# Revit family: HPL-BA-300-xxxx-xxx-PC
name_source: partatom
category: Oprawy oświetleniowe
revit_build: Autodesk Revit 2017 (Build: 20190507_1515(x64)
units: mm (PartAtom-declared; Revit-internal decimal feet)

## family parameters
Numer OmniClass = 23.80.70.11
Obiekt nadrzędny = Powierzchnia
Punkt obliczania pomieszczeń = Nie
Tnij formami wycięć po wczytaniu = Nie
Typ części = Normalny
Tytuł OmniClass = Luminaries for Internal Lighting
Współdzielony = Nie
Wymiar okrągłego złącza = Użyj średnicy
Źródło światła = Tak

## types (12) — shared parameters
Emituj kształt widoczny w renderingu = Nie
Emituj ze średnicy okręgu = 305 mm  [stored 1.00066 ft]
Filtr koloru = 16777215
Kod zespołu = D5020200
Lampa = LED
Odchylenie kierunku = 90.00°
Producent = RIDI Leuchten GmbH
URL = www.ridi.de
Zmiana temperatury barwowej przyciemniania lampy = <Brak>
brand = RIDI
conformity mark = CE
electrical safety class = 1
height = 300 mm
ingress protection (IP) code = IP20
length = 315 mm  [stored 1.03346 ft]
nominal frequency = 50-60Hz
nominal voltage = 230
voltage type (AC, DC, UC) = AC
width = 315 mm  [stored 1.03346 ft]
zero-valued in all types: Domyślna rzędna

## per-type parameters (varying)
| type | Model | Obciążenie pozorne | Plik sieci fotometrycznej | rated input power | weight |
| HPL-BA 300/6000-830 PC | 0321493 | 55 VA | HPL-BA 300_6000 PM_PC.IES | 55 | 3,4 kg |
| HPL-BA 300/6000-830 PC-DALI | 0331493 | 55 VA | HPL-BA 300_6000 PM_PC.IES | 55 | 3,29 kg |
| HPL-BA 300/6000-840 PC | 0321494 | 55 VA | HPL-BA 300_6000 PM_PC.IES | 55 | 3,29 kg |
| HPL-BA 300/6000-840 PC-DALI | 0331494 | 55 VA | HPL-BA 300_6000 PM_PC.IES | 55 | 3,29 kg |
| HPL-BA 300/9000-830 PC-DALI | 0331495 | 70 VA | HPL-BA 300_9000 PM_PC.IES | 70 | 3,4 kg |
| HPL-BA 300/9000-840 PC | 0321496 | 70 VA | HPL-BA 300_9000 PM_PC.IES | 70 | 3,4 kg |
| HPL-BA 300/9000-840 PC-DALI | 0331496 | 70 VA | HPL-BA 300_9000 PM_PC.IES | 70 | 3,4 kg |
| HPL-BA 300/11000-830 PC | 0321425 | 87 VA | HPL-BA 300_11000 PM_PC.IES | 87 | 3,4 kg |
| HPL-BA 300/9000-830 PC | 0321495 | 70 VA | HPL-BA 300_9000 PM_PC.IES | 70 | 3,4 kg |
| HPL-BA 300/11000-830 PC-DALI | 0331425 | 87 VA | HPL-BA 300_11000 PM_PC.IES | 87 | 3,66 kg |
| HPL-BA 300/11000-840 PC | 0321422 | 87 VA | HPL-BA 300_11000 PM_PC.IES | 87 | 3,66 kg |
| HPL-BA 300/11000-840 PC-DALI | 0331422 | 87 VA | HPL-BA 300_11000 PM_PC.IES | 87 | 3,66 kg |

note: column(s) folded — value = type name in every type: product name

note: [stored X ft] marks values corroborated as IEEE doubles in the binary element streams (Revit-internal decimal feet)
